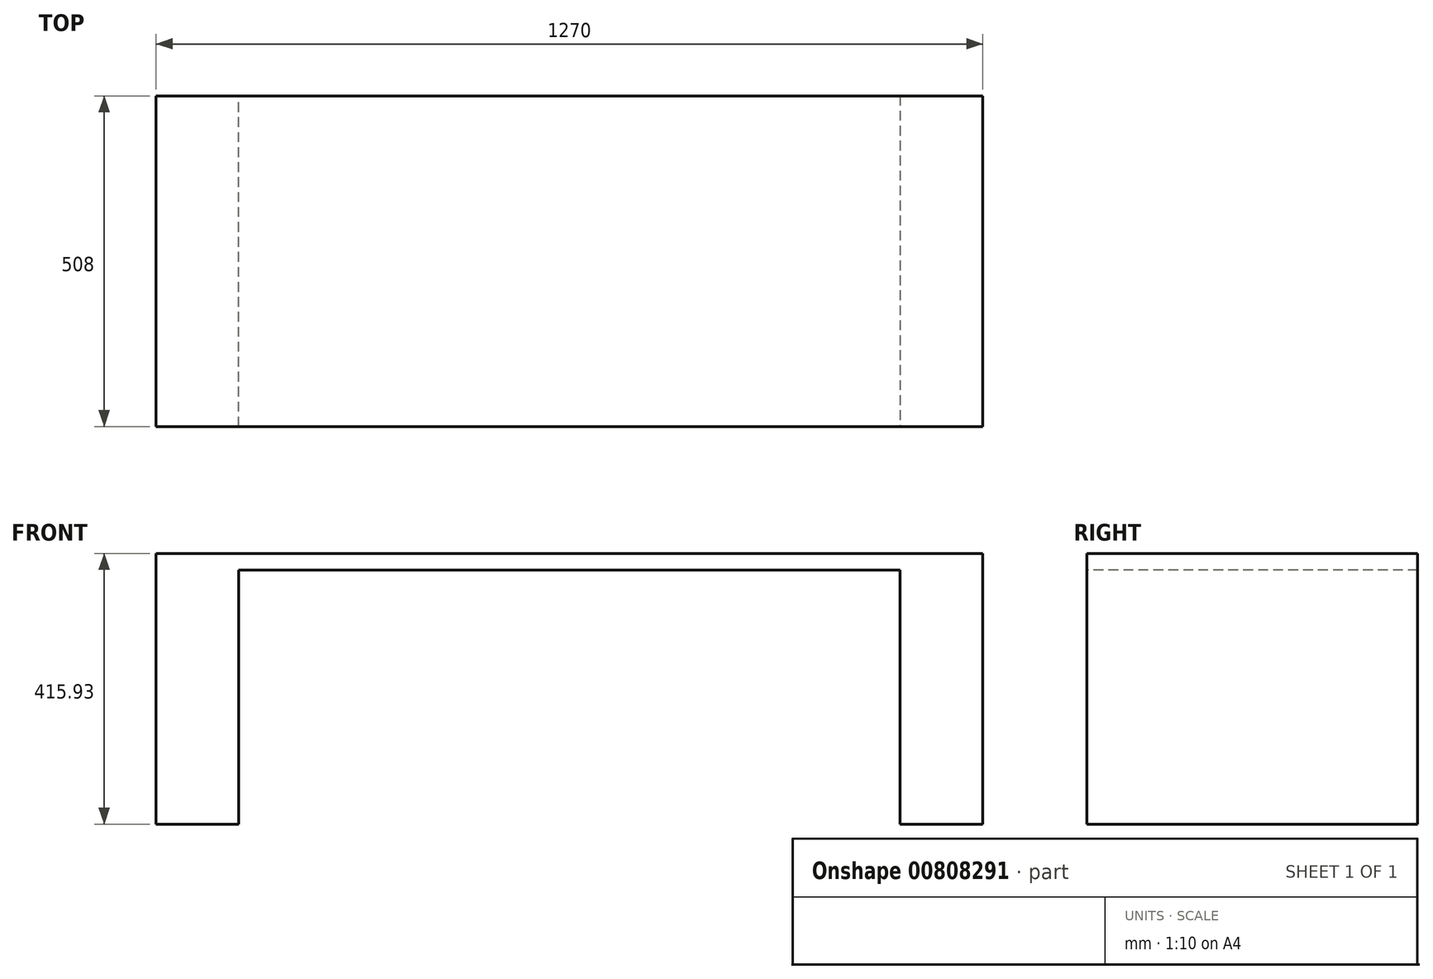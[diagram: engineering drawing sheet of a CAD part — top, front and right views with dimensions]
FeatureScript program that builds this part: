
annotation { "Feature Type Name" : "Feature", "Feature Type Description" : "" }
export const myFeature = defineFeature(function(context is Context, id is Id, definition is map)
    precondition{}
    {
        {
            var Q0;
            Q0=qCreatedBy(makeId("Top.planeOp"),FACE);
            var sketch = newSketch(context, id + "F0", { "sketchPlane" : qUnion([Q0])});
            skLineSegment(sketch, "E0.bottom", {"start": v(635, -254) * mm, "end": v(-635, -254) * mm});
            skLineSegment(sketch, "E0.top", {"start": v(635, 254) * mm, "end": v(-635, 254) * mm});
            skLineSegment(sketch, "E0.left", {"start": v(635, -254) * mm, "end": v(635, 254) * mm});
            skLineSegment(sketch, "E0.right", {"start": v(-635, -254) * mm, "end": v(-635, 254) * mm});
            skPoint(sketch, "E0.middle", {"position": v(0, 0) * mm});
            skSolve(sketch);
        }
        {
            var Q0;
            Q0=qSketchRegion(id+"F0",true);
            extrude(context, id + "F1", {"entities" : qUnion([Q0]), "depth" : 25.4 * mm, "offsetDistance" : 25.4 * mm});
        }
        {
            var Q0;
            Q0=makeQuery(id+"F1.opExtrude","CAP_FACE",FACE,{"disambiguationData":[OSD([sQuery(id+"F0.wireOp",EDGE,"E0.bottom"),sQuery(id+"F0.wireOp",EDGE,"E0.top"),sQuery(id+"F0.wireOp",EDGE,"E0.left"),sQuery(id+"F0.wireOp",EDGE,"E0.right")])],"isStart":true});
            var sketch = newSketch(context, id + "F2", { "sketchPlane" : qUnion([Q0])});
            skLineSegment(sketch, "E1.bottom", {"start": v(-635, 254) * mm, "end": v(-508, 254) * mm});
            skLineSegment(sketch, "E1.top", {"start": v(-635, -254) * mm, "end": v(-508, -254) * mm});
            skLineSegment(sketch, "E1.left", {"start": v(-635, 254) * mm, "end": v(-635, -254) * mm});
            skLineSegment(sketch, "E1.right", {"start": v(-508, 254) * mm, "end": v(-508, -254) * mm});
            skLineSegment(sketch, "E2.bottom", {"start": v(635, -254) * mm, "end": v(508, -254) * mm});
            skLineSegment(sketch, "E2.top", {"start": v(635, 254) * mm, "end": v(508, 254) * mm});
            skLineSegment(sketch, "E2.left", {"start": v(635, -254) * mm, "end": v(635, 254) * mm});
            skLineSegment(sketch, "E2.right", {"start": v(508, -254) * mm, "end": v(508, 254) * mm});
            skSolve(sketch);
        }
        {
            var Q0;
            Q0=qSketchRegion(id+"F2",true);
            extrude(context, id + "F3", {"entities" : qUnion([Q0]), "operationType" : NewBodyOperationType.ADD, "depth" : 390.52 * mm, "offsetDistance" : 25.4 * mm});
        }
    });
